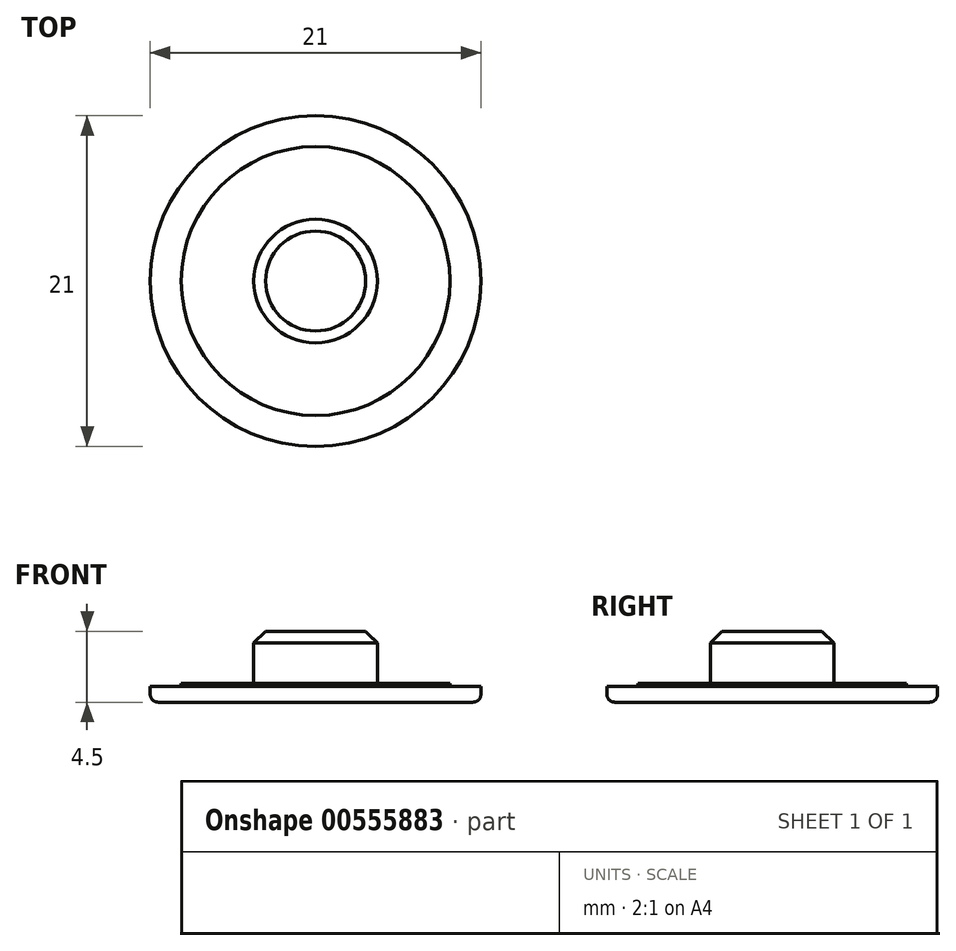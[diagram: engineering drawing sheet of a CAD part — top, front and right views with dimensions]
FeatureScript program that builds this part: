
annotation { "Feature Type Name" : "Feature", "Feature Type Description" : "" }
export const myFeature = defineFeature(function(context is Context, id is Id, definition is map)
    precondition{}
    {
        {
            var Q0;
            Q0=qCreatedBy(makeId("Top.planeOp"),FACE);
            var sketch = newSketch(context, id + "F0", { "sketchPlane" : qUnion([Q0])});
            skCircle(sketch, "E0", {"center": v(0, 0) * mm, "radius": 10.5 * mm});
            skSolve(sketch);
        }
        {
            var Q0;
            Q0=makeQuery(id+"F0.imprint","IMPRINT",FACE,{"disambiguationData":[TD([[makeQuery(id+"F0.imprint","IMPRINT",EDGE,{"derivedFrom":sQuery(id+"F0.wireOp",EDGE,"E0")}),1.0]])]});
            extrude(context, id + "F1", {"entities" : qUnion([Q0]), "depth" : 1 * mm, "offsetDistance" : 25 * mm});
        }
        {
            var Q0;
            Q0=makeQuery(id+"F1.opExtrude","CAP_FACE",FACE,{"disambiguationData":[OSD([sQuery(id+"F0.wireOp",EDGE,"E0")])],"isStart":false});
            var sketch = newSketch(context, id + "F2", { "sketchPlane" : qUnion([Q0])});
            skCircle(sketch, "E1", {"center": v(0, 0) * mm, "radius": 3.92 * mm});
            skSolve(sketch);
        }
        {
            var Q0;
            Q0 = qSketchRegion(id + "F2", true);
            extrude(context, id + "F3", {"entities" : qUnion([Q0]), "operationType" : NewBodyOperationType.ADD, "depth" : 3.5 * mm, "offsetDistance" : 25 * mm});
        }
        {
            var Q0;
            Q0=makeQuery(id+"F3.opExtrude","CAP_EDGE",EDGE,{"disambiguationData":[OSD([sQuery(id+"F2.wireOp",EDGE,"E1")])],"isStart":false});
            chamfer(context, id + "F4", {"entities" : qUnion([Q0]), "width" : .75 * mm, "tangentPropagation" : true});
        }
        {
            var Q0;
            Q0=makeQuery(id+"F1.opExtrude","CAP_EDGE",EDGE,{"disambiguationData":[OSD([sQuery(id+"F0.wireOp",EDGE,"E0")])],"isStart":true});
            fillet(context, id + "F5", {"entities" : qUnion([Q0]), "radius" : .5 * mm, "tangentPropagation" : true, "allowEdgeOverflow" : false});
        }
        {
            var Q0;
            Q0=makeQuery(id+"F1.opExtrude","CAP_FACE",FACE,{"disambiguationData":[OSD([sQuery(id+"F0.wireOp",EDGE,"E0")])],"isStart":false});
            var sketch = newSketch(context, id + "F6", { "sketchPlane" : qUnion([Q0])});
            skCircle(sketch, "E2", {"center": v(0, 0) * mm, "radius": 8.54 * mm});
            skSolve(sketch);
        }
        {
            var Q0;
            Q0 = qSketchRegion(id + "F6", true);
            extrude(context, id + "F7", {"entities" : qUnion([Q0]), "operationType" : NewBodyOperationType.ADD, "depth" : .2 * mm, "offsetDistance" : 25 * mm});
        }
    });
